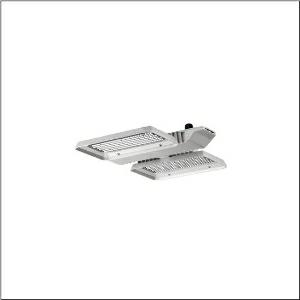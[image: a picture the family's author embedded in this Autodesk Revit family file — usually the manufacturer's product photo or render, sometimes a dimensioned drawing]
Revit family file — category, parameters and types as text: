
# Revit family: highbay_11_51hla1d14fca
name_source: partatom
category: Lighting Fixtures
units: mm (PartAtom-declared; Revit-internal decimal feet)

## family parameters
Cut with Voids When Loaded = No
Host = Face
Light Source = No
Part Type = Normal
Room Calculation Point = No
Round Connector Dimension = Use Diameter
Shared = No

## types (1)
- --- (1 x LED, 14060 lm, 81.2 W, 4000K)
    Apparent Load = 81 VA
    CIE Flux Codes = 88 95 99 100 99
    Color Rendering = 80
    Color Temperature = 4000K
    Default Elevation = 1800 mm
    Description = Highbay 11, LED high bay luminaire, primary light control with lens, of PMMA, light emission: direct distribution, primary light characteristic: symmetric, installation type: surface-mounted, suspended mounting, for 1x 2 x LED rated luminous flux: 14.060 lm, light colour: 840, colour temperature: 4000K, control gear: ECG DALI, with terminal, 5-pole, max. 2.5mm², mains connection: 230..240V, AC, 50/60Hz, rated input power: 81W, LED unit, of diecast aluminium, unplated, bead blasted, silver, length: 470 mm, width: 500 mm, height: 65mm, housing, of diecast aluminium, uncoated, bead blasted, silver, protection rating (complete): IP65, insulation class (complete): insulation class I (protective earthing), certification: CE, ENEC, VDE, protection symbol: D, impact resistance: IK08 with glass or PC cover, permissible ambient temperature for indoor applications: -35..+55°C, reducing of maximum allowable ambient temperature of 5°C with ceiling mounting, corresponds to IFS (International Featured Standards) requirements for safety and quality in the food industry, packaging unit: 1 piece
    Height = 95 mm
    Lamp = 1 x LED
    Lamp Light Flux = 14060 lm
    Lamp Power = 81.2 W
    Lamp count = 1
    Length = 468 mm
    Luminous efficacy = 173 lm/W
    Manufacturer = Siteco
    ModVariant = No
    Model = 51HLA1D14FCA
    Mounting Place = Ceiling
    Mounting Type = Pendant
    Number of Poles = 1
    OnlyDefault = Yes
    Power Factor = 1
    Product Name = Highbay 11
    Product group = LED high bay luminaire
    ProductGroupID = 903
    Protection Class = Protection class I
    Protection Degree = IP 65
    RLX_Detail_Level = 1
    RlxData = <blob elided: 89405 chars, md5=115fde30>
    Socket = socket
    Standby Power = 0 W
    System Light Flux = 14060 lm
    System Power = 81 W
    Type Comments = factory setting: luminous flux: 100 % | dim-lin: 254 | 460 mA
    Type Image = l_1003425.jpg
    URL = http://relux.com
    VarID = @adj_141163
    Voltage = 0 V
    Weight = 0.00 kg
    Width = 501 mm

## geometry (parser evidence)
native form markers: Blend x4, Sweep x11
no freeform markers — native parametric forms only
